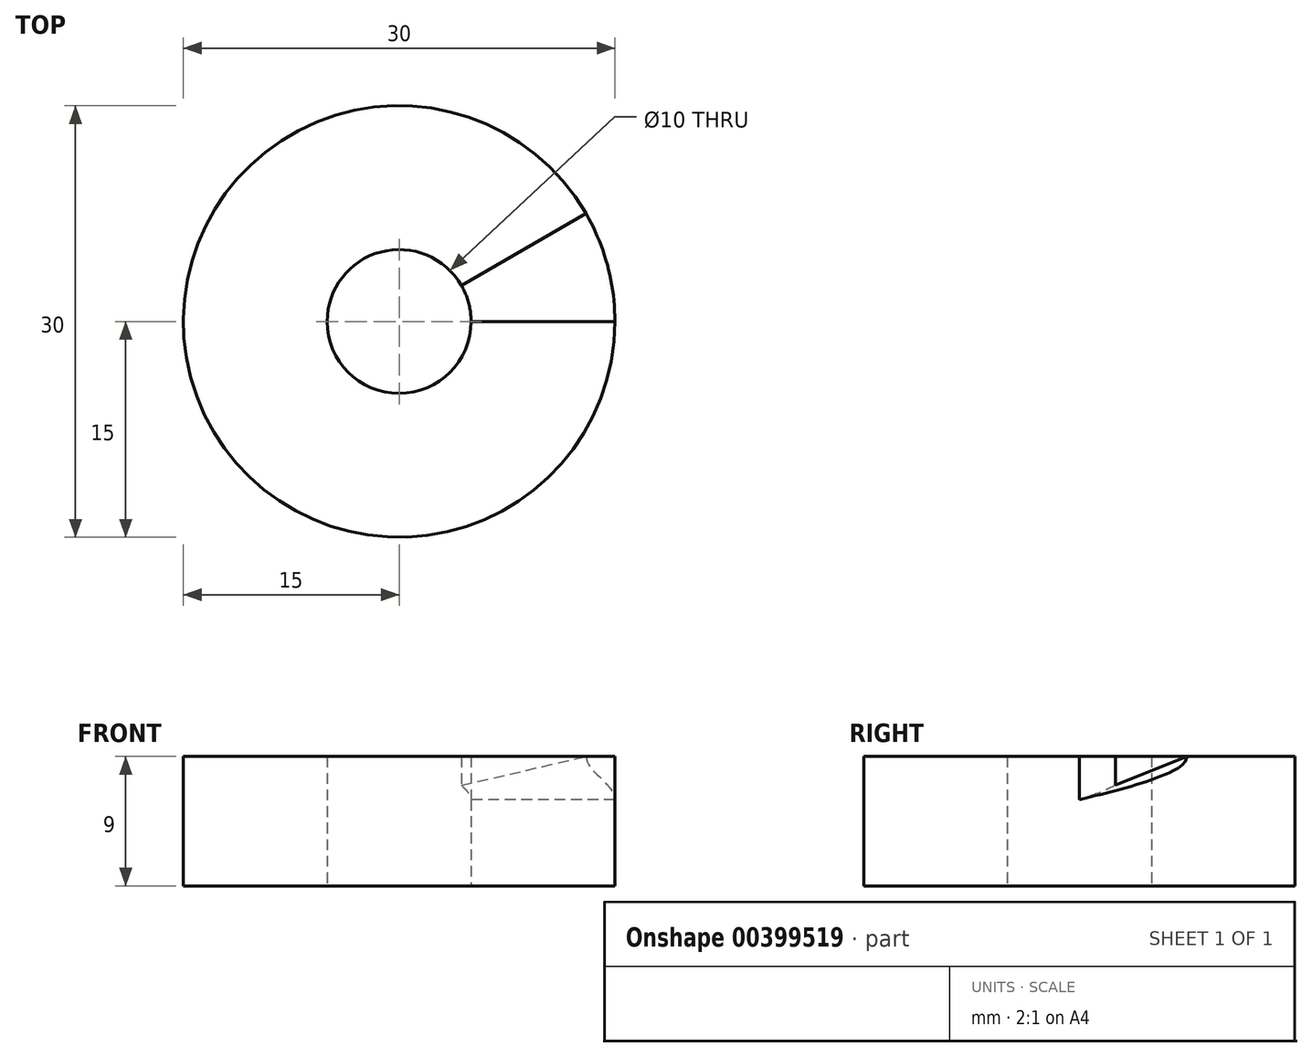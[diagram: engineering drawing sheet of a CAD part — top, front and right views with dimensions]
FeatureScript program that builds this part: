
annotation { "Feature Type Name" : "Feature", "Feature Type Description" : "" }
export const myFeature = defineFeature(function(context is Context, id is Id, definition is map)
    precondition{}
    {
        {
            var Q0;
            Q0=qCreatedBy(makeId("Top.planeOp"),FACE);
            var sketch = newSketch(context, id + "F0", { "sketchPlane" : qUnion([Q0])});
            skCircle(sketch, "E0", {"center": v(0, 0) * mm, "radius": 15 * mm});
            skSolve(sketch);
        }
        {
            var Q0;
            Q0 = qSketchRegion(id + "F0", true);
            extrude(context, id + "F1", {"entities" : qUnion([Q0]), "depth" : 9 * mm});
        }
        {
            var Q0;
            Q0=qCreatedBy(makeId("Front.planeOp"),FACE);
            var sketch = newSketch(context, id + "F2", { "sketchPlane" : qUnion([Q0])});
            skLineSegment(sketch, "E1", {"start": v(15, 6) * mm, "end": v(15, 9) * mm});
            skLineSegment(sketch, "E2", {"start": v(15, 9) * mm, "end": v(0, 9) * mm});
            skLineSegment(sketch, "E3.0", {"start": v(-15, 9) * mm, "end": v(15, 9) * mm, "construction": true});
            skLineSegment(sketch, "E4", {"start": v(15, 6) * mm, "end": v(0, 6) * mm});
            skLineSegment(sketch, "E5", {"start": v(0, 6) * mm, "end": v(0, 9) * mm});
            skSolve(sketch);
        }
        {
            var Q0;
            Q0=makeQuery(id+"F1.opExtrude","CAP_FACE",FACE,{"disambiguationData":[OSD([sQuery(id+"F0.wireOp",EDGE,"E0")])],"isStart":false});
            var sketch = newSketch(context, id + "F3", { "sketchPlane" : qUnion([Q0])});
            skLineSegment(sketch, "E6", {"start": v(0, 0) * mm, "end": v(13, 7.5) * mm});
            skLineSegment(sketch, "E7", {"start": v(0, 0) * mm, "end": v(0, 0) * mm});
            skSolve(sketch);
        }
        {
            var Q0;
            Q0=sQuery(id+"F2.wireOp",EDGE,"E3.0");
            cPoint(context, id + "F4", {"entities" : qUnion([Q0]), "parameter" : 0.5});
        }
        {
            var Q0;
            Q0 = qCreatedBy(id + "F4" ,VERTEX);
            var Q1;
            Q1=sQuery(id+"F3.wireOp",VERTEX,"E6.end");
            var Q2;
            Q2=qCreatedBy(makeId("Origin.pointOp"),VERTEX);
            cPlane(context, id + "F5", {"entities" : qUnion([Q0, Q1, Q2]), "cplaneType" : CPlaneType.THREE_POINT, "offset" : 25 * mm, "width" : 150 * mm, "height" : 150 * mm});
        }
        {
            var Q0;
            Q0=qCreatedBy(id+"F5.planeOp",FACE);
            var sketch = newSketch(context, id + "F6", { "sketchPlane" : qUnion([Q0])});
            skLineSegment(sketch, "E8.0", {"start": v(0, 9) * mm, "end": v(15, 9) * mm});
            skLineSegment(sketch, "E9", {"start": v(25, 15.2) * mm, "end": v(25, 9) * mm});
            skLineSegment(sketch, "E10", {"start": v(25, 9) * mm, "end": v(15, 9) * mm});
            skLineSegment(sketch, "E11", {"start": v(0, 9) * mm, "end": v(25, 15.2) * mm});
            skLineSegment(sketch, "E12", {"start": v(0, 9) * mm, "end": v(0, 0) * mm, "construction": true});
            skSolve(sketch);
        }
        {
            var Q1;
            Q1 = qSketchRegion(id + "F2", true);
            var Q2;
            Q2 = qSketchRegion(id + "F6", true);
            loft(context, id + "F7", {"operationType" : NewBodyOperationType.REMOVE, "sheetProfilesArray" : [{ "sheetProfileEntities" : qUnion([Q1]) }, { "sheetProfileEntities" : qUnion([Q2]) }]});
        }
        {
            var Q0;
            Q0=makeQuery(id+"F1.opExtrude","CAP_FACE",FACE,{"disambiguationData":[OSD([sQuery(id+"F0.wireOp",EDGE,"E0")])],"isStart":true});
            var sketch = newSketch(context, id + "F8", { "sketchPlane" : qUnion([Q0])});
            skCircle(sketch, "E13", {"center": v(0, 0) * mm, "radius": 5 * mm});
            skSolve(sketch);
        }
        {
            var Q0;
            Q0 = qSketchRegion(id + "F8", true);
            extrude(context, id + "F9", {"entities" : qUnion([Q0]), "operationType" : NewBodyOperationType.REMOVE, "oppositeDirection" : true, "depth" : 25 * mm});
        }
    });
